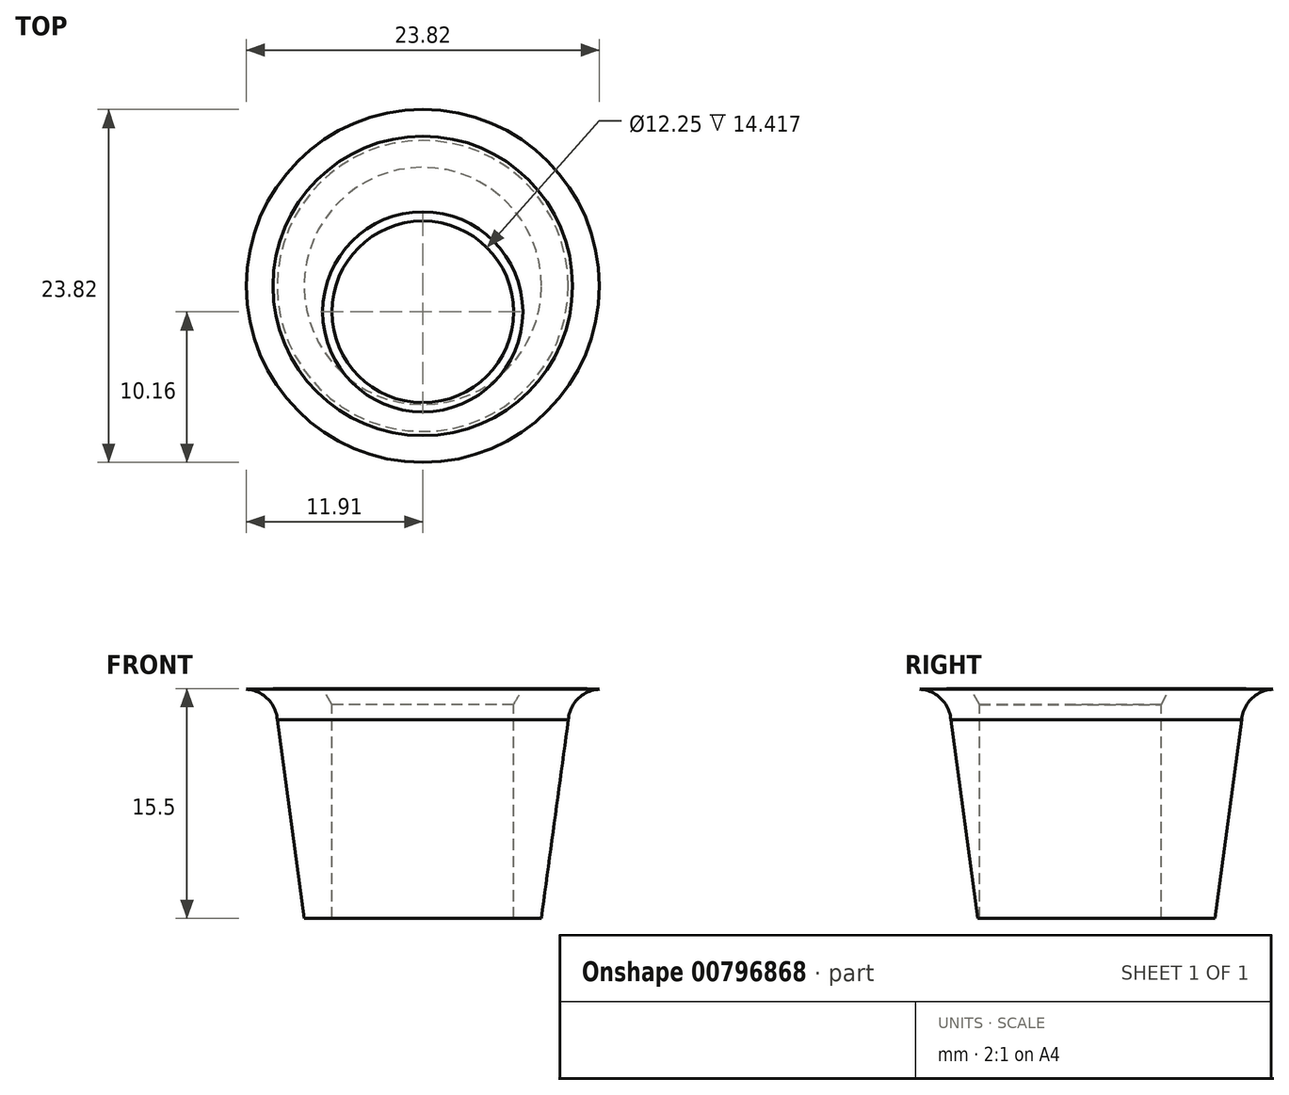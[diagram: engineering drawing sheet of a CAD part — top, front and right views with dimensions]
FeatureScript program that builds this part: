
annotation { "Feature Type Name" : "Feature", "Feature Type Description" : "" }
export const myFeature = defineFeature(function(context is Context, id is Id, definition is map)
    precondition{}
    {
        {
            var Q0;
            Q0=qCreatedBy(makeId("Front.planeOp"),FACE);
            var sketch = newSketch(context, id + "F0", { "sketchPlane" : qUnion([Q0])});
            skLineSegment(sketch, "E0", {"start": v(0, 0) * mm, "end": v(0, -15.5) * mm});
            skLineSegment(sketch, "E1", {"start": v(0, -15.5) * mm, "end": v(8, -15.5) * mm});
            skLineSegment(sketch, "E2", {"start": v(0, 0) * mm, "end": v(10.1, 0) * mm});
            skLineSegment(sketch, "E3", {"start": v(10.1, 0) * mm, "end": v(8, -15.5) * mm});
            skPoint(sketch, "E4", {"position": v(0, 0) * mm});
            skArc(sketch, "E5", {"start": v(9.82, -2.1) * mm, "mid": v(10.47, -0.68) * mm, "end": v(11.9, -0.05) * mm});
            skLineSegment(sketch, "E6", {"start": v(11.9, -0.05) * mm, "end": v(10.1, 0) * mm});
            skSolve(sketch);
        }
        {
            var Q0;
            Q0=makeQuery(id+"F0.imprint","IMPRINT",FACE,{"disambiguationData":[TD([[makeQuery(id+"F0.imprint","IMPRINT",EDGE,{"derivedFrom":sQuery(id+"F0.wireOp",EDGE,"E0")}),1.0]])]});
            var Q1;
            {var subQ0=sQuery(id+"F0.wireOp",EDGE,"E6");Q1=makeQuery(id+"F0.imprint","IMPRINT",FACE,{"disambiguationData":[TD([[makeQuery(id+"F0.imprint","IMPRINT",EDGE,{"derivedFrom":subQ0}),1.0]])]});}
            var Q2;
            Q2=sQuery(id+"F0.wireOp",EDGE,"E3");
            var Q3;
            Q3=sQuery(id+"F0.wireOp",EDGE,"E2");
            var Q4;
            Q4=sQuery(id+"F0.wireOp",EDGE,"E1");
            var Q5;
            Q5=sQuery(id+"F0.wireOp",EDGE,"E0");
            revolve(context, id + "F1", {"surfaceOperationType" : NewSurfaceOperationType.NEW, "entities" : qUnion([Q0, Q1]), "surfaceEntities" : qUnion([Q2, Q3, Q4]), "axis" : qUnion([Q5]), "revolveType" : RevolveType.FULL});
        }
        {
            var Q0;
            Q0=qCreatedBy(makeId("Top.planeOp"),FACE);
            var sketch = newSketch(context, id + "F2", { "sketchPlane" : qUnion([Q0])});
            skPoint(sketch, "E7", {"position": v(0, 0) * mm});
            skPoint(sketch, "E8", {"position": v(0, -1.75) * mm});
            skSolve(sketch);
        }
        {
            var Q0;
            Q0=sQuery(id+"F2.wireOp",VERTEX,"E8");
            var Q1;
            Q1=makeQuery(id+"F1.opRevolve","SWEPT_BODY",BODY,{"disambiguationData":[OSD([sQuery(id+"F0.wireOp",EDGE,"E0"),sQuery(id+"F0.wireOp",EDGE,"E1"),sQuery(id+"F0.wireOp",EDGE,"E2"),sQuery(id+"F0.wireOp",EDGE,"E3")])]});
            hole(context, id + "F3", {"style" : HoleStyle.C_SINK, "endStyle" : HoleEndStyle.THROUGH, "holeDiameter" : 12.25 * mm, "cSinkDiameter" : 13.5 * mm, "cSinkAngle" : 60 * degree, "majorDiameter" : 5 * mm, "isTappedThrough" : true, "tappedDepth" : 12 * mm, "tapClearance" : 3, "startFromSketch" : true, "locations" : qUnion([Q0]), "scope" : qUnion([Q1])});
        }
    });
